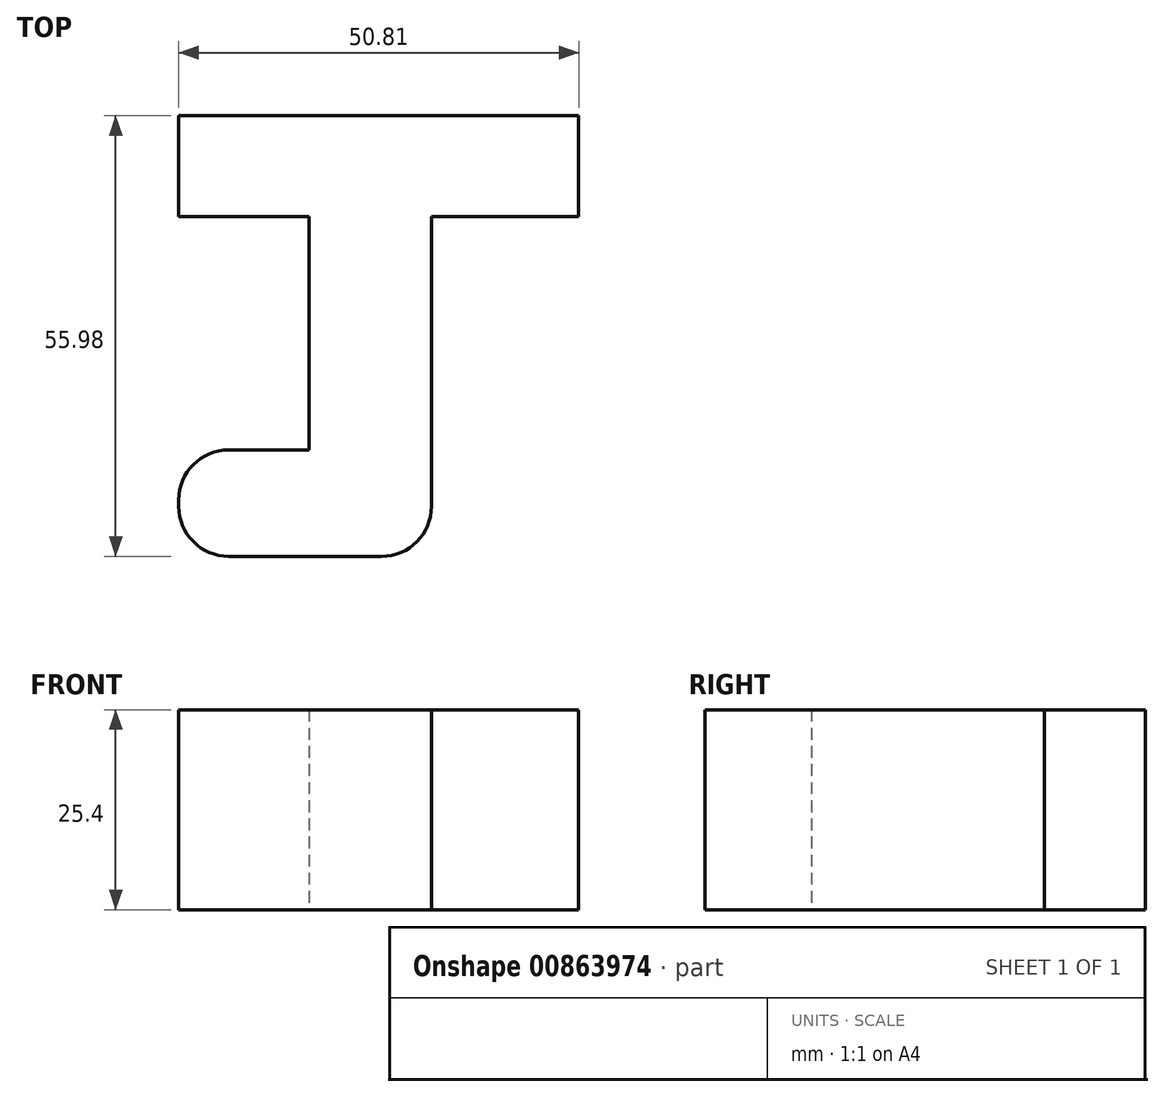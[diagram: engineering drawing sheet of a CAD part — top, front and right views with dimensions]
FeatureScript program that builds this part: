
annotation { "Feature Type Name" : "Feature", "Feature Type Description" : "" }
export const myFeature = defineFeature(function(context is Context, id is Id, definition is map)
    precondition{}
    {
        {
            var Q0;
            Q0=qCreatedBy(makeId("Top.planeOp"),FACE);
            var sketch = newSketch(context, id + "F0", { "sketchPlane" : qUnion([Q0])});
            skLineSegment(sketch, "E0", {"start": v(0, 0) * mm, "end": v(50.8, 0) * mm});
            skLineSegment(sketch, "E1", {"start": v(50.8, 0) * mm, "end": v(50.8, -12.8) * mm});
            skLineSegment(sketch, "E2", {"start": v(50.8, -12.8) * mm, "end": v(32.1, -12.8) * mm});
            skLineSegment(sketch, "E3", {"start": v(32.1, -12.8) * mm, "end": v(32.1, -42.45) * mm});
            skLineSegment(sketch, "E4", {"start": v(0, 0) * mm, "end": v(0, -12.8) * mm});
            skLineSegment(sketch, "E5", {"start": v(0, -12.8) * mm, "end": v(16.56, -12.8) * mm});
            skLineSegment(sketch, "E6", {"start": v(16.56, -12.8) * mm, "end": v(16.56, -42.45) * mm});
            skLineSegment(sketch, "E7", {"start": v(16.56, -42.45) * mm, "end": v(6.35, -42.45) * mm});
            skLineSegment(sketch, "E8", {"start": v(0, -48.8) * mm, "end": v(0, -49.63) * mm});
            skLineSegment(sketch, "E9", {"start": v(6.35, -55.98) * mm, "end": v(25.75, -55.98) * mm});
            skLineSegment(sketch, "E10", {"start": v(32.1, -49.63) * mm, "end": v(32.1, -42.45) * mm});
            skPoint(sketch, "E11.visualSharp", {"position": v(32.1, -55.98) * mm});
            skArc(sketch, "E11.filletArc", {"start": v(25.75, -55.98) * mm, "mid": v(30.24, -54.12) * mm, "end": v(32.1, -49.63) * mm});
            skPoint(sketch, "E12.visualSharp", {"position": v(0, -42.45) * mm});
            skArc(sketch, "E12.filletArc", {"start": v(6.35, -42.45) * mm, "mid": v(1.86, -44.31) * mm, "end": v(0, -48.8) * mm});
            skPoint(sketch, "E13.visualSharp", {"position": v(0, -55.98) * mm});
            skArc(sketch, "E13.filletArc", {"start": v(0, -49.63) * mm, "mid": v(1.86, -54.12) * mm, "end": v(6.35, -55.98) * mm});
            skSolve(sketch);
        }
        {
            var Q0;
            Q0=makeQuery(id+"F0.imprint","IMPRINT",FACE,{"disambiguationData":[TD([[makeQuery(id+"F0.imprint","IMPRINT",EDGE,{"derivedFrom":sQuery(id+"F0.wireOp",EDGE,"E0")}),-1.0]])]});
            extrude(context, id + "F1", {"entities" : qUnion([Q0]), "depth" : 25.4 * mm, "offsetDistance" : 25.4 * mm});
        }
    });
